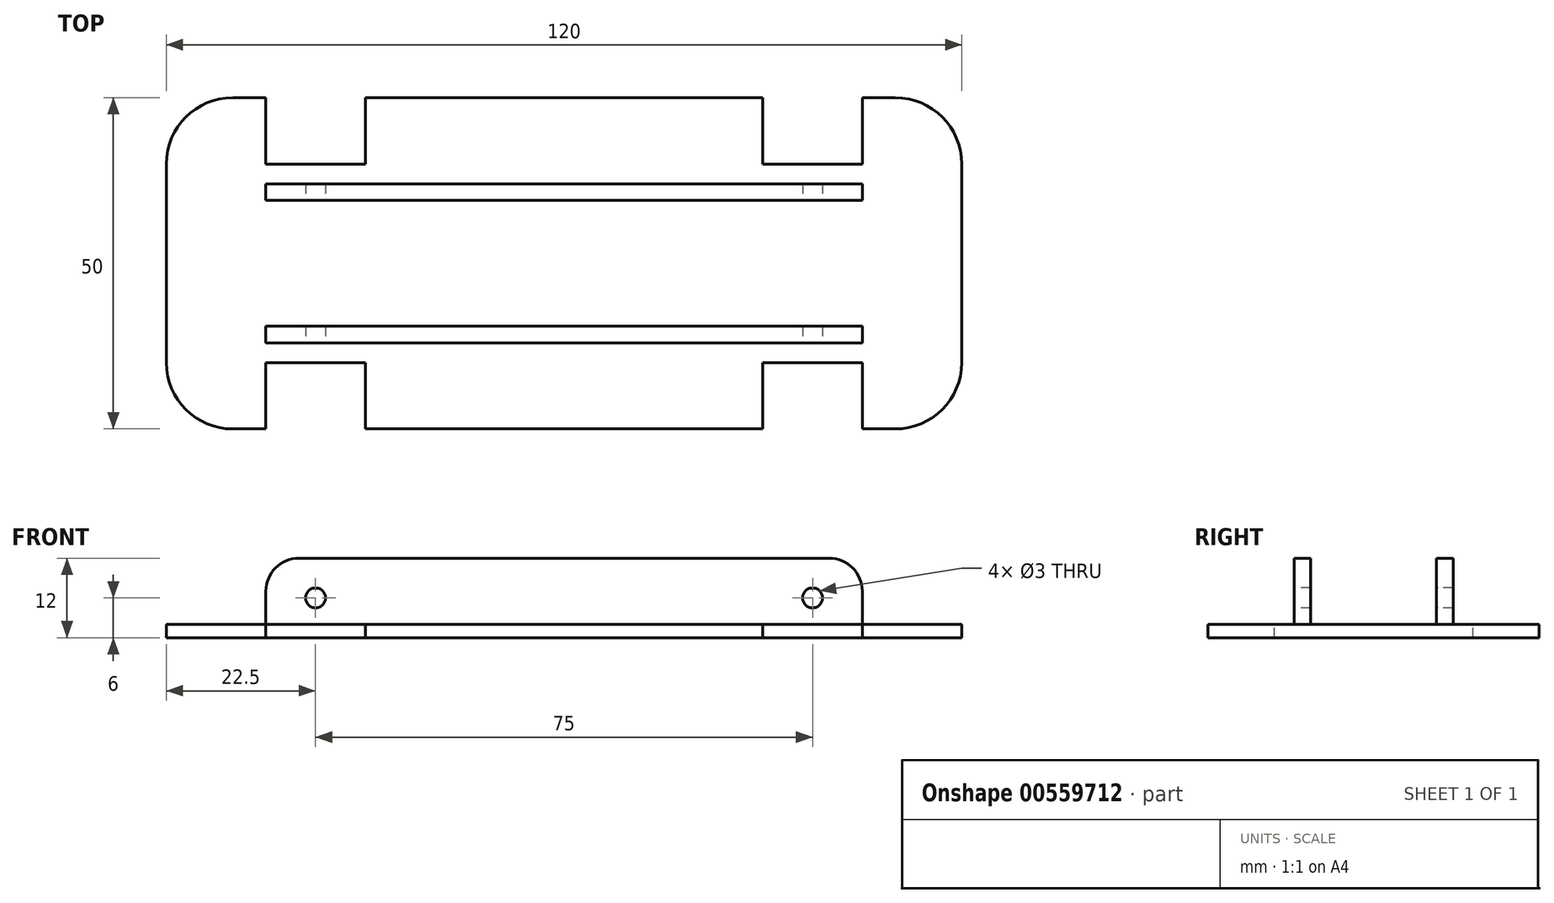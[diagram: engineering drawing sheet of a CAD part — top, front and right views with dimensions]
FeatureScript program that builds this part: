
annotation { "Feature Type Name" : "Feature", "Feature Type Description" : "" }
export const myFeature = defineFeature(function(context is Context, id is Id, definition is map)
    precondition{}
    {
        {
            var Q0;
            Q0=qCreatedBy(makeId("Top.planeOp"),FACE);
            var sketch = newSketch(context, id + "F0", { "sketchPlane" : qUnion([Q0])});
            skLineSegment(sketch, "E0.bottom", {"start": v(60, -25) * mm, "end": v(-60, -25) * mm});
            skLineSegment(sketch, "E0.top", {"start": v(60, 25) * mm, "end": v(-60, 25) * mm});
            skLineSegment(sketch, "E0.left", {"start": v(60, -25) * mm, "end": v(60, 25) * mm});
            skLineSegment(sketch, "E0.right", {"start": v(-60, -25) * mm, "end": v(-60, 25) * mm});
            skPoint(sketch, "E0.middle", {"position": v(0, 0) * mm});
            skSolve(sketch);
        }
        {
            var Q0;
            Q0=makeQuery(id+"F0.imprint","IMPRINT",FACE,{"disambiguationData":[TD([[makeQuery(id+"F0.imprint","IMPRINT",EDGE,{"derivedFrom":sQuery(id+"F0.wireOp",EDGE,"E0.bottom")}),-1.0]])]});
            extrude(context, id + "F1", {"entities" : qUnion([Q0]), "depth" : 2 * mm, "offsetDistance" : 25 * mm});
        }
        {
            var Q0;
            Q0=makeQuery(id+"F1.opExtrude","CAP_FACE",FACE,{"disambiguationData":[OSD([sQuery(id+"F0.wireOp",EDGE,"E0.bottom"),sQuery(id+"F0.wireOp",EDGE,"E0.top"),sQuery(id+"F0.wireOp",EDGE,"E0.left"),sQuery(id+"F0.wireOp",EDGE,"E0.right")])],"isStart":false});
            var sketch = newSketch(context, id + "F2", { "sketchPlane" : qUnion([Q0])});
            skLineSegment(sketch, "E1.bottom", {"start": v(30, -25) * mm, "end": v(45, -25) * mm});
            skLineSegment(sketch, "E1.top", {"start": v(30, -15) * mm, "end": v(45, -15) * mm});
            skLineSegment(sketch, "E1.left", {"start": v(30, -25) * mm, "end": v(30, -15) * mm});
            skLineSegment(sketch, "E1.right", {"start": v(45, -25) * mm, "end": v(45, -15) * mm});
            skSolve(sketch);
        }
        {
            var Q0;
            Q0=makeQuery(id+"F2.imprint","IMPRINT",FACE,{"disambiguationData":[TD([[makeQuery(id+"F2.imprint","IMPRINT",EDGE,{"derivedFrom":sQuery(id+"F2.wireOp",EDGE,"E1.bottom")}),-1.0]])]});
            extrude(context, id + "F3", {"entities" : qUnion([Q0]), "operationType" : NewBodyOperationType.REMOVE, "oppositeDirection" : true, "depth" : 25 * mm, "offsetDistance" : 25 * mm});
        }
        {
            var Q0;
            Q0=makeQuery(id+"F1.opExtrude","CAP_FACE",FACE,{"disambiguationData":[OSD([sQuery(id+"F0.wireOp",EDGE,"E0.bottom"),sQuery(id+"F0.wireOp",EDGE,"E0.top"),sQuery(id+"F0.wireOp",EDGE,"E0.left"),sQuery(id+"F0.wireOp",EDGE,"E0.right")])],"isStart":false});
            var sketch = newSketch(context, id + "F4", { "sketchPlane" : qUnion([Q0])});
            skLineSegment(sketch, "E2.bottom", {"start": v(30, 25) * mm, "end": v(45, 25) * mm});
            skLineSegment(sketch, "E2.top", {"start": v(30, 15) * mm, "end": v(45, 15) * mm});
            skLineSegment(sketch, "E2.left", {"start": v(30, 25) * mm, "end": v(30, 15) * mm});
            skLineSegment(sketch, "E2.right", {"start": v(45, 25) * mm, "end": v(45, 15) * mm});
            skSolve(sketch);
        }
        {
            var Q0;
            Q0=makeQuery(id+"F4.imprint","IMPRINT",FACE,{"disambiguationData":[TD([[makeQuery(id+"F4.imprint","IMPRINT",EDGE,{"derivedFrom":sQuery(id+"F4.wireOp",EDGE,"E2.bottom")}),1.0]])]});
            extrude(context, id + "F5", {"entities" : qUnion([Q0]), "operationType" : NewBodyOperationType.REMOVE, "endBound" : BoundingType.SYMMETRIC, "oppositeDirection" : true, "depth" : 25 * mm, "offsetDistance" : 25 * mm});
        }
        {
            var Q0;
            Q0=makeQuery(id+"F1.opExtrude","CAP_FACE",FACE,{"disambiguationData":[OSD([sQuery(id+"F0.wireOp",EDGE,"E0.bottom"),sQuery(id+"F0.wireOp",EDGE,"E0.top"),sQuery(id+"F0.wireOp",EDGE,"E0.left"),sQuery(id+"F0.wireOp",EDGE,"E0.right")])],"isStart":false});
            var sketch = newSketch(context, id + "F6", { "sketchPlane" : qUnion([Q0])});
            skLineSegment(sketch, "E3.bottom", {"start": v(-45, 25) * mm, "end": v(-30, 25) * mm});
            skLineSegment(sketch, "E3.top", {"start": v(-45, 15) * mm, "end": v(-30, 15) * mm});
            skLineSegment(sketch, "E3.left", {"start": v(-45, 25) * mm, "end": v(-45, 15) * mm});
            skLineSegment(sketch, "E3.right", {"start": v(-30, 25) * mm, "end": v(-30, 15) * mm});
            skSolve(sketch);
        }
        {
            var Q0;
            Q0=makeQuery(id+"F6.imprint","IMPRINT",FACE,{"disambiguationData":[TD([[makeQuery(id+"F6.imprint","IMPRINT",EDGE,{"derivedFrom":sQuery(id+"F6.wireOp",EDGE,"E3.bottom")}),1.0]])]});
            extrude(context, id + "F7", {"entities" : qUnion([Q0]), "operationType" : NewBodyOperationType.REMOVE, "oppositeDirection" : true, "depth" : 25 * mm, "offsetDistance" : 25 * mm});
        }
        {
            var Q0;
            Q0=makeQuery(id+"F1.opExtrude","CAP_FACE",FACE,{"disambiguationData":[OSD([sQuery(id+"F0.wireOp",EDGE,"E0.bottom"),sQuery(id+"F0.wireOp",EDGE,"E0.top"),sQuery(id+"F0.wireOp",EDGE,"E0.left"),sQuery(id+"F0.wireOp",EDGE,"E0.right")])],"isStart":false});
            var sketch = newSketch(context, id + "F8", { "sketchPlane" : qUnion([Q0])});
            skLineSegment(sketch, "E4.bottom", {"start": v(-45, -25) * mm, "end": v(-30, -25) * mm});
            skLineSegment(sketch, "E4.top", {"start": v(-45, -15) * mm, "end": v(-30, -15) * mm});
            skLineSegment(sketch, "E4.left", {"start": v(-45, -25) * mm, "end": v(-45, -15) * mm});
            skLineSegment(sketch, "E4.right", {"start": v(-30, -25) * mm, "end": v(-30, -15) * mm});
            skSolve(sketch);
        }
        {
            var Q0;
            Q0=makeQuery(id+"F8.imprint","IMPRINT",FACE,{"disambiguationData":[TD([[makeQuery(id+"F8.imprint","IMPRINT",EDGE,{"derivedFrom":sQuery(id+"F8.wireOp",EDGE,"E4.bottom")}),-1.0]])]});
            extrude(context, id + "F9", {"entities" : qUnion([Q0]), "operationType" : NewBodyOperationType.REMOVE, "oppositeDirection" : true, "depth" : 25 * mm, "offsetDistance" : 25 * mm});
        }
        {
            var Q0;
            Q0=makeQuery(id+"F1.opExtrude","CAP_FACE",FACE,{"disambiguationData":[OSD([sQuery(id+"F0.wireOp",EDGE,"E0.bottom"),sQuery(id+"F0.wireOp",EDGE,"E0.top"),sQuery(id+"F0.wireOp",EDGE,"E0.left"),sQuery(id+"F0.wireOp",EDGE,"E0.right")])],"isStart":false});
            var sketch = newSketch(context, id + "F10", { "sketchPlane" : qUnion([Q0])});
            skLineSegment(sketch, "E5.bottom", {"start": v(-45, -12) * mm, "end": v(45, -12) * mm});
            skLineSegment(sketch, "E5.top", {"start": v(-45, -9.5) * mm, "end": v(45, -9.5) * mm});
            skLineSegment(sketch, "E5.left", {"start": v(-45, -12) * mm, "end": v(-45, -9.5) * mm});
            skLineSegment(sketch, "E5.right", {"start": v(45, -12) * mm, "end": v(45, -9.5) * mm});
            skSolve(sketch);
        }
        {
            var Q0;
            Q0=makeQuery(id+"F10.imprint","IMPRINT",FACE,{"disambiguationData":[TD([[makeQuery(id+"F10.imprint","IMPRINT",EDGE,{"derivedFrom":sQuery(id+"F10.wireOp",EDGE,"E5.bottom")}),1.0]])]});
            extrude(context, id + "F11", {"entities" : qUnion([Q0]), "operationType" : NewBodyOperationType.ADD, "depth" : 10 * mm, "offsetDistance" : 25 * mm});
        }
        {
            var Q0;
            Q0=makeQuery(id+"F1.opExtrude","CAP_FACE",FACE,{"disambiguationData":[OSD([sQuery(id+"F0.wireOp",EDGE,"E0.bottom"),sQuery(id+"F0.wireOp",EDGE,"E0.top"),sQuery(id+"F0.wireOp",EDGE,"E0.left"),sQuery(id+"F0.wireOp",EDGE,"E0.right")])],"isStart":false});
            var sketch = newSketch(context, id + "F12", { "sketchPlane" : qUnion([Q0])});
            skLineSegment(sketch, "E6.bottom", {"start": v(-45, 12) * mm, "end": v(45, 12) * mm});
            skLineSegment(sketch, "E6.top", {"start": v(-45, 9.5) * mm, "end": v(45, 9.5) * mm});
            skLineSegment(sketch, "E6.left", {"start": v(-45, 12) * mm, "end": v(-45, 9.5) * mm});
            skLineSegment(sketch, "E6.right", {"start": v(45, 12) * mm, "end": v(45, 9.5) * mm});
            skSolve(sketch);
        }
        {
            var Q0;
            Q0=makeQuery(id+"F12.imprint","IMPRINT",FACE,{"disambiguationData":[TD([[makeQuery(id+"F12.imprint","IMPRINT",EDGE,{"derivedFrom":sQuery(id+"F12.wireOp",EDGE,"E6.bottom")}),-1.0]])]});
            extrude(context, id + "F13", {"entities" : qUnion([Q0]), "operationType" : NewBodyOperationType.ADD, "depth" : 10 * mm, "offsetDistance" : 25 * mm});
        }
        {
            var Q0;
            Q0=makeQuery(id+"F11.opExtrude","CAP_EDGE",EDGE,{"disambiguationData":[OSD([sQuery(id+"F10.wireOp",EDGE,"E5.left")])],"isStart":false});
            fillet(context, id + "F14", {"entities" : qUnion([Q0]), "radius" : 5 * mm, "tangentPropagation" : true, "allowEdgeOverflow" : false});
        }
        {
            var Q0;
            Q0=makeQuery(id+"F13.opExtrude","CAP_EDGE",EDGE,{"disambiguationData":[OSD([sQuery(id+"F12.wireOp",EDGE,"E6.right")])],"isStart":false});
            var Q1;
            Q1=makeQuery(id+"F13.opExtrude","CAP_EDGE",EDGE,{"disambiguationData":[OSD([sQuery(id+"F12.wireOp",EDGE,"E6.left")])],"isStart":false});
            var Q2;
            Q2=makeQuery(id+"F11.opExtrude","CAP_EDGE",EDGE,{"disambiguationData":[OSD([sQuery(id+"F10.wireOp",EDGE,"E5.right")])],"isStart":false});
            fillet(context, id + "F15", {"entities" : qUnion([Q0, Q1, Q2]), "radius" : 5 * mm, "tangentPropagation" : true, "allowEdgeOverflow" : false});
        }
        {
            var Q0;
            Q0=makeQuery(id+"F1.opExtrude","SWEPT_EDGE",EDGE,{"disambiguationData":[OSD([sQuery(id+"F0.wireOp",EDGE,"E0.bottom"),sQuery(id+"F0.wireOp",EDGE,"E0.left")])]});
            var Q1;
            Q1=makeQuery(id+"F1.opExtrude","SWEPT_EDGE",EDGE,{"disambiguationData":[OSD([sQuery(id+"F0.wireOp",EDGE,"E0.top"),sQuery(id+"F0.wireOp",EDGE,"E0.left")])]});
            fillet(context, id + "F16", {"entities" : qUnion([Q0, Q1]), "radius" : 10 * mm, "tangentPropagation" : true, "allowEdgeOverflow" : false});
        }
        {
            var Q0;
            Q0=makeQuery(id+"F1.opExtrude","SWEPT_EDGE",EDGE,{"disambiguationData":[OSD([sQuery(id+"F0.wireOp",EDGE,"E0.bottom"),sQuery(id+"F0.wireOp",EDGE,"E0.right")])]});
            var Q1;
            Q1=makeQuery(id+"F1.opExtrude","SWEPT_EDGE",EDGE,{"disambiguationData":[OSD([sQuery(id+"F0.wireOp",EDGE,"E0.top"),sQuery(id+"F0.wireOp",EDGE,"E0.right")])]});
            fillet(context, id + "F17", {"entities" : qUnion([Q0, Q1]), "radius" : 10 * mm, "tangentPropagation" : true, "allowEdgeOverflow" : false});
        }
        {
            var Q0;
            Q0=makeQuery(id+"F11.opExtrude","SWEPT_FACE",FACE,{"disambiguationData":[OSD([sQuery(id+"F10.wireOp",EDGE,"E5.bottom")])]});
            var sketch = newSketch(context, id + "F18", { "sketchPlane" : qUnion([Q0])});
            skCircle(sketch, "E7", {"center": v(-37.5, 6) * mm, "radius": 1.5 * mm});
            skCircle(sketch, "E8", {"center": v(37.5, 6) * mm, "radius": 1.5 * mm});
            skSolve(sketch);
        }
        {
            var Q0;
            Q0=makeQuery(id+"F18.imprint","IMPRINT",FACE,{"disambiguationData":[TD([[makeQuery(id+"F18.imprint","IMPRINT",EDGE,{"derivedFrom":sQuery(id+"F18.wireOp",EDGE,"E7")}),1.0]])]});
            var Q1;
            Q1=sQuery(id+"F18.wireOp",EDGE,"E7");
            extrude(context, id + "F19", {"entities" : qUnion([Q0]), "operationType" : NewBodyOperationType.REMOVE, "surfaceEntities" : qUnion([Q1]), "endBound" : BoundingType.THROUGH_ALL, "oppositeDirection" : true, "depth" : 25 * mm, "offsetDistance" : 25 * mm});
        }
        {
            var Q0;
            Q0 = qSketchRegion(id + "F18", true);
            extrude(context, id + "F20", {"entities" : qUnion([Q0]), "operationType" : NewBodyOperationType.REMOVE, "oppositeDirection" : true, "depth" : 25 * mm, "offsetDistance" : 25 * mm});
        }
    });
